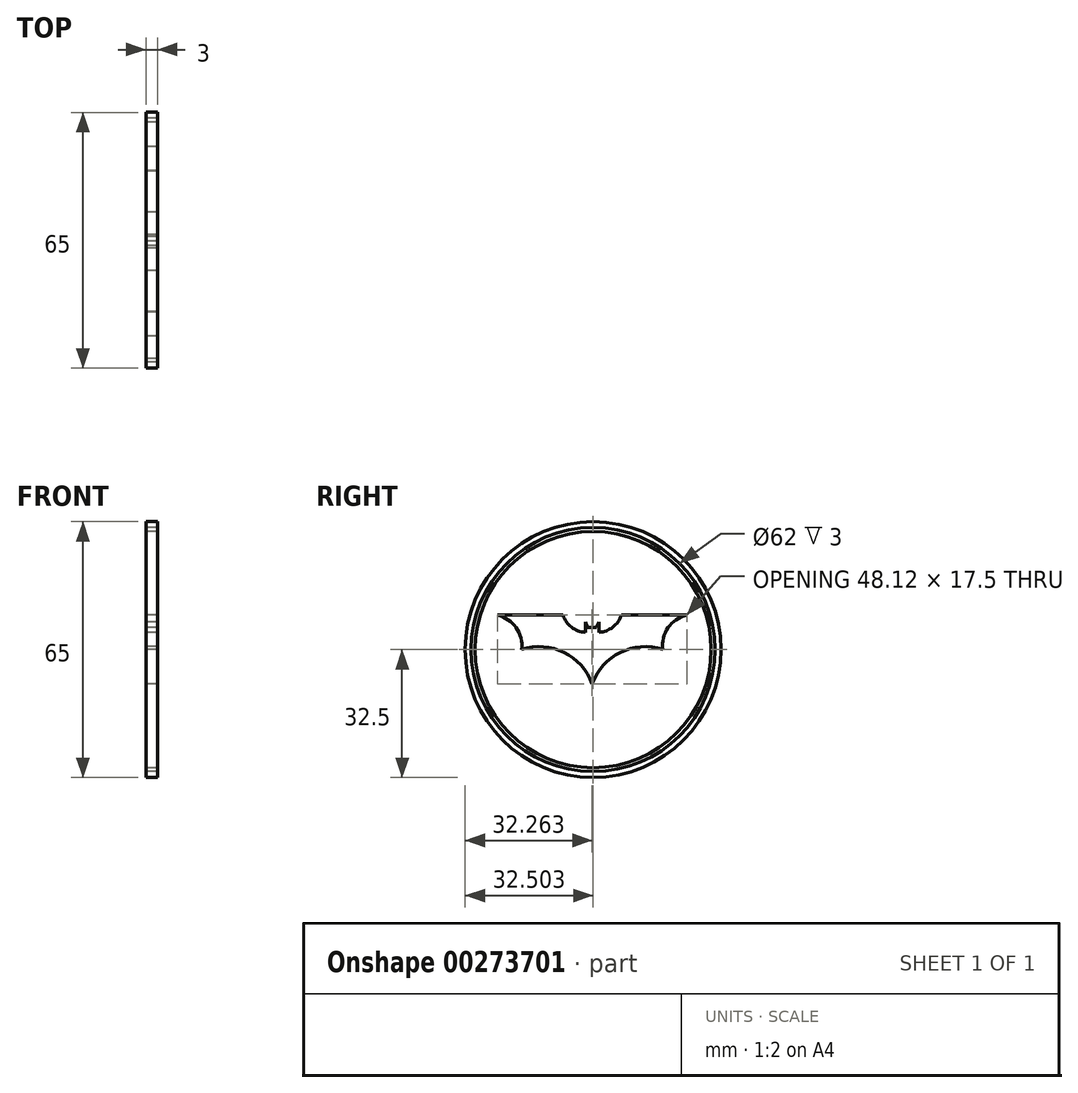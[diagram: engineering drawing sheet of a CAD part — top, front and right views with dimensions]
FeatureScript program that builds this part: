
annotation { "Feature Type Name" : "Feature", "Feature Type Description" : "" }
export const myFeature = defineFeature(function(context is Context, id is Id, definition is map)
    precondition{}
    {
        {
            var Q0;
            Q0=qCreatedBy(makeId("Right.planeOp"),FACE);
            var sketch = newSketch(context, id + "F0", { "sketchPlane" : qUnion([Q0])});
            skLineSegment(sketch, "E0.top", {"start": v(0, 17.5) * mm, "end": v(16.62, 17.5) * mm});
            skPoint(sketch, "E1.second.point", {"position": v(-4.77, 10.26) * mm});
            skPoint(sketch, "E1.third.point", {"position": v(7.12, 14.8) * mm});
            skPoint(sketch, "E2.startSnap0", {"position": v(0, 8.75) * mm});
            skArc(sketch, "E3", {"start": v(6.12, 8.75) * mm, "mid": v(4.77, 14.32) * mm, "end": v(0, 17.5) * mm});
            skArc(sketch, "E4", {"start": v(24.06, 0) * mm, "mid": v(16.9, 8.06) * mm, "end": v(6.12, 8.75) * mm});
            skLineSegment(sketch, "E5", {"start": v(22.31, 15.75) * mm, "end": v(22.31, 13.12) * mm});
            skArc(sketch, "E6", {"start": v(16.62, 17.5) * mm, "mid": v(18.81, 14.46) * mm, "end": v(22.31, 13.12) * mm});
            skLineSegment(sketch, "E7", {"start": v(22.31, 15.75) * mm, "end": v(22.94, 14.38) * mm});
            skLineSegment(sketch, "E8", {"start": v(22.94, 14.38) * mm, "end": v(24.06, 14.38) * mm});
            skLineSegment(sketch, "E9.MirrorCS", {"start": v(25.19, 14.38) * mm, "end": v(24.06, 14.38) * mm});
            skLineSegment(sketch, "E10.MirrorCS", {"start": v(25.81, 15.75) * mm, "end": v(25.19, 14.38) * mm});
            skLineSegment(sketch, "E11.MirrorCS", {"start": v(25.81, 15.75) * mm, "end": v(25.81, 13.12) * mm});
            skArc(sketch, "E12.MirrorCS", {"start": v(31.5, 17.5) * mm, "mid": v(29.31, 14.46) * mm, "end": v(25.81, 13.12) * mm});
            skLineSegment(sketch, "E13.MirrorCS", {"start": v(48.12, 17.5) * mm, "end": v(31.5, 17.5) * mm});
            skArc(sketch, "E14.MirrorCS", {"start": v(42, 8.75) * mm, "mid": v(43.35, 14.32) * mm, "end": v(48.12, 17.5) * mm});
            skArc(sketch, "E15.MirrorCS", {"start": v(24.06, 0) * mm, "mid": v(31.23, 8.06) * mm, "end": v(42, 8.75) * mm});
            skPoint(sketch, "E16.orphan", {"position": v(48.12, 0) * mm});
            skPoint(sketch, "E17.start.orphan", {"position": v(0, 0) * mm});
            skLineSegment(sketch, "E18.trimOffspring", {"start": v(31.5, 17.5) * mm, "end": v(48.12, 17.5) * mm});
            skPoint(sketch, "E19.orphan", {"position": v(24.06, 17.5) * mm});
            skCircle(sketch, "E20", {"center": v(24.3, 8.75) * mm, "radius": 30 * mm});
            skCircle(sketch, "E21", {"center": v(24.3, 8.75) * mm, "radius": 31 * mm});
            skCircle(sketch, "E22", {"center": v(24.3, 8.75) * mm, "radius": 32.5 * mm});
            skSolve(sketch);
        }
        {
            var Q0;
            Q0=makeQuery(id+"F0.imprint","IMPRINT",FACE,{"disambiguationData":[TD([[makeQuery(id+"F0.imprint","IMPRINT",EDGE,{"derivedFrom":sQuery(id+"F0.wireOp",EDGE,"E3")}),1.0]])]});
            var Q1;
            Q1=makeQuery(id+"F0.imprint","IMPRINT",FACE,{"disambiguationData":[TD([[makeQuery(id+"F0.imprint","IMPRINT",EDGE,{"derivedFrom":sQuery(id+"F0.wireOp",EDGE,"E21")}),-1.0]])]});
            extrude(context, id + "F1", {"entities" : qUnion([Q0, Q1]), "depth" : 3 * mm});
        }
    });
